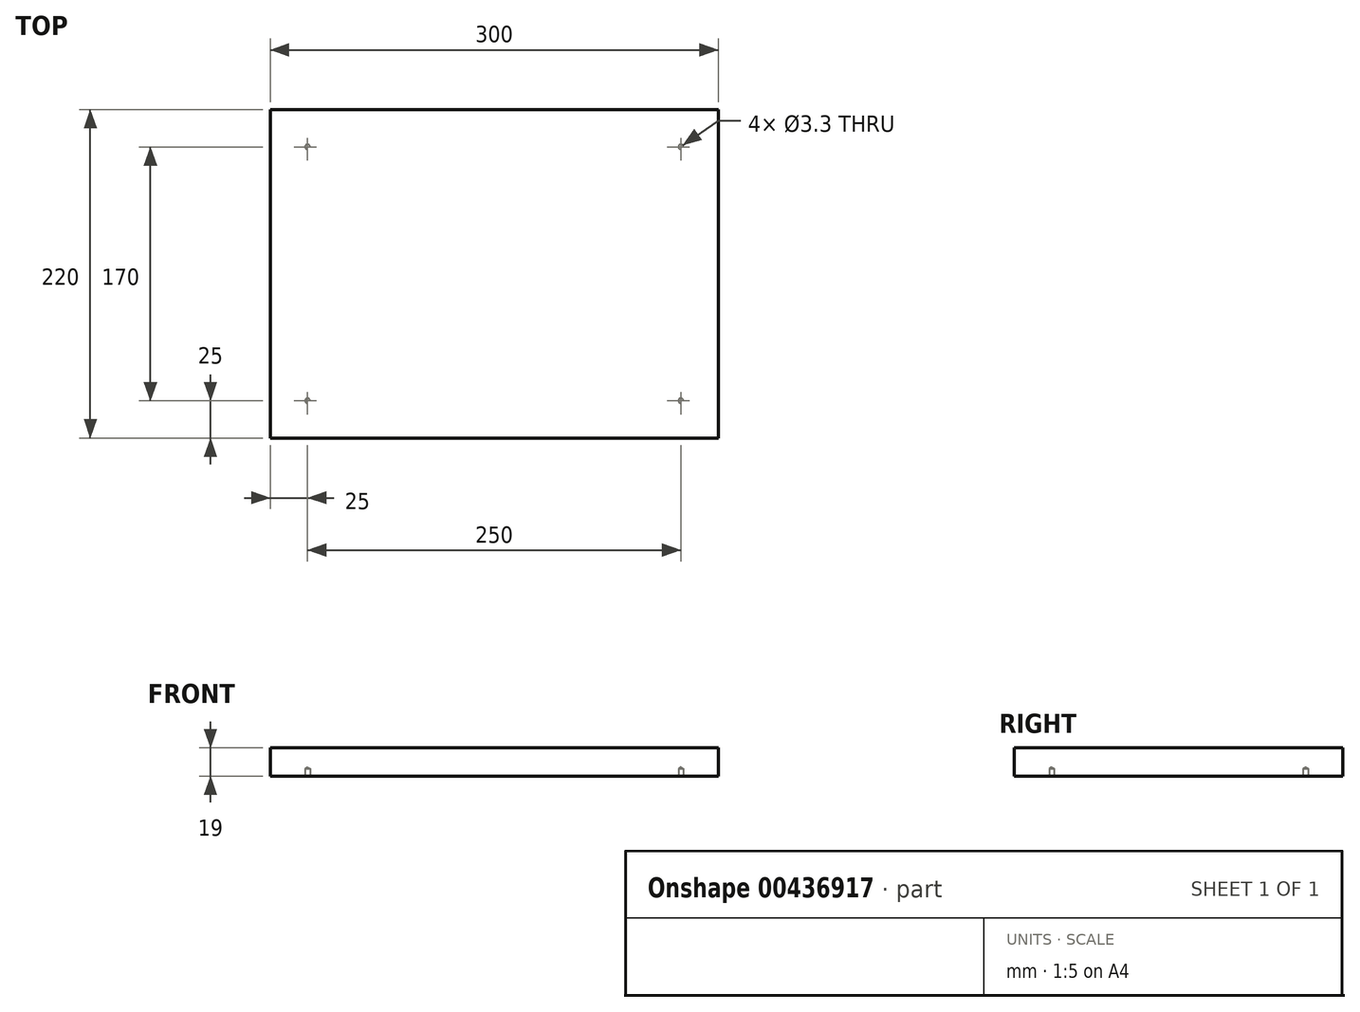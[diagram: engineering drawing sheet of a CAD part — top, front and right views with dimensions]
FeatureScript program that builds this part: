
annotation { "Feature Type Name" : "Feature", "Feature Type Description" : "" }
export const myFeature = defineFeature(function(context is Context, id is Id, definition is map)
    precondition{}
    {
        {
            var Q0;
            Q0=qCreatedBy(makeId("Top.planeOp"),FACE);
            var sketch = newSketch(context, id + "F0", { "sketchPlane" : qUnion([Q0])});
            skLineSegment(sketch, "E0.bottom", {"start": v(0, 0) * mm, "end": v(300, 0) * mm});
            skLineSegment(sketch, "E0.top", {"start": v(0, 220) * mm, "end": v(300, 220) * mm});
            skLineSegment(sketch, "E0.left", {"start": v(0, 0) * mm, "end": v(0, 220) * mm});
            skLineSegment(sketch, "E0.right", {"start": v(300, 0) * mm, "end": v(300, 220) * mm});
            skSolve(sketch);
        }
        {
            var Q0;
            Q0 = qSketchRegion(id + "F0", true);
            extrude(context, id + "F1", {"entities" : qUnion([Q0]), "depth" : 19 * mm});
        }
        {
            var Q0;
            Q0=makeQuery(id+"F1.opExtrude","CAP_FACE",FACE,{"disambiguationData":[OSD([sQuery(id+"F0.wireOp",EDGE,"E0.bottom"),sQuery(id+"F0.wireOp",EDGE,"E0.top"),sQuery(id+"F0.wireOp",EDGE,"E0.left"),sQuery(id+"F0.wireOp",EDGE,"E0.right")])],"isStart":true});
            var sketch = newSketch(context, id + "F2", { "sketchPlane" : qUnion([Q0])});
            skPoint(sketch, "E1", {"position": v(25, -25) * mm});
            skPoint(sketch, "E2", {"position": v(25, -195) * mm});
            skPoint(sketch, "E3", {"position": v(275, -195) * mm});
            skPoint(sketch, "E4", {"position": v(275, -25) * mm});
            skSolve(sketch);
        }
        {
            var Q0;
            Q0=sQuery(id+"F2.wireOp",VERTEX,"E1");
            var Q1;
            Q1=sQuery(id+"F2.wireOp",VERTEX,"E2");
            var Q2;
            Q2=sQuery(id+"F2.wireOp",VERTEX,"E3");
            var Q3;
            Q3=sQuery(id+"F2.wireOp",VERTEX,"E4");
            var Q4;
            Q4=makeQuery(id+"F1.opExtrude","SWEPT_BODY",BODY,{"disambiguationData":[OSD([sQuery(id+"F0.wireOp",EDGE,"E0.bottom"),sQuery(id+"F0.wireOp",EDGE,"E0.top"),sQuery(id+"F0.wireOp",EDGE,"E0.left"),sQuery(id+"F0.wireOp",EDGE,"E0.right")])]});
            hole(context, id + "F3", {"style" : HoleStyle.SIMPLE, "endStyle" : HoleEndStyle.BLIND, "standardTappedOrClearance" : lookupTablePath({ "standard" : "ISO", "fit" : "Normal", "size" : "M3", "type" : "Clearance" }), "standardBlindInLast" : lookupTablePath({ "fit" : "Standard", "standard" : "ISO", "size" : "M3", "type" : "Clearance" }), "holeDiameter" : 3.3 * mm, "holeDepth" : 5 * mm, "isTappedThrough" : true, "tappedDepth" : 12 * mm, "tapClearance" : 3, "locations" : qUnion([Q0, Q1, Q2, Q3]), "scope" : qUnion([Q4])});
        }
    });
